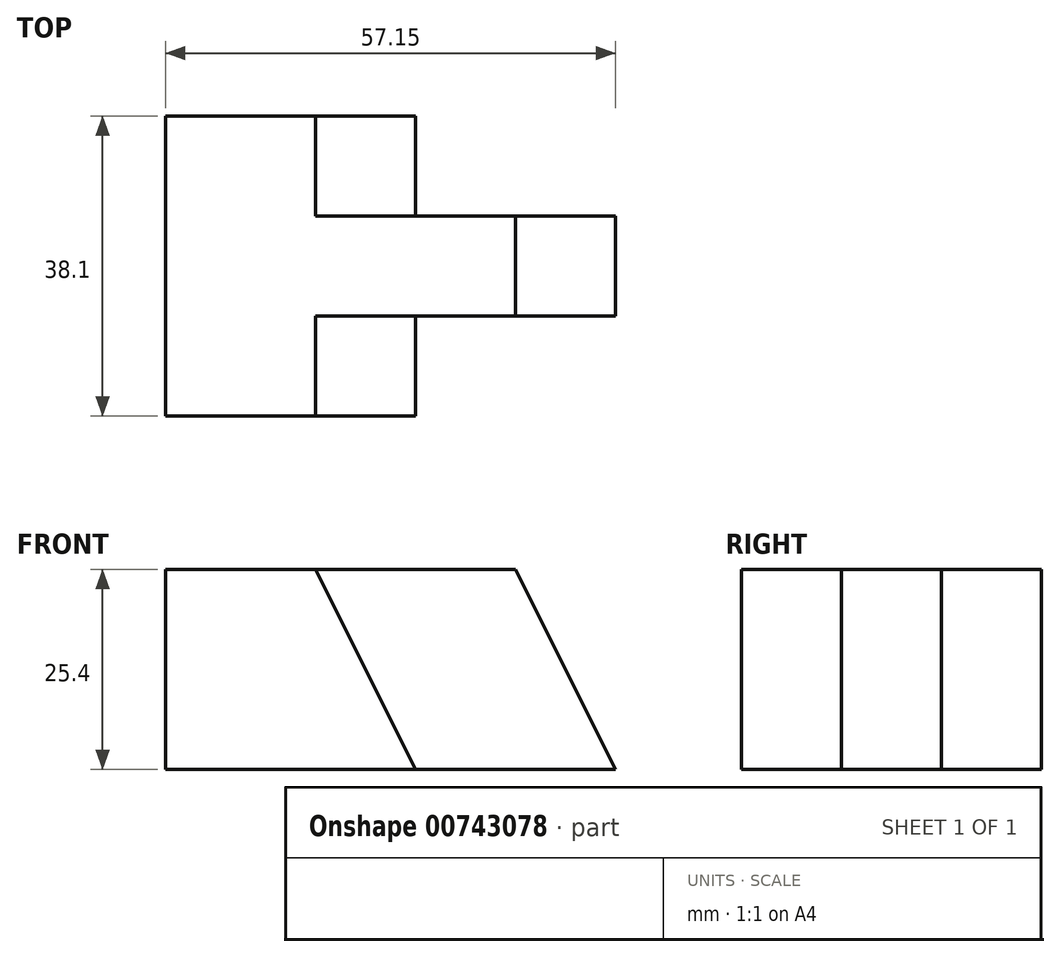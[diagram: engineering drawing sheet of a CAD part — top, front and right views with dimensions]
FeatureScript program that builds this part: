
annotation { "Feature Type Name" : "Feature", "Feature Type Description" : "" }
export const myFeature = defineFeature(function(context is Context, id is Id, definition is map)
    precondition{}
    {
        {
            var Q0;
            Q0=qCreatedBy(makeId("Top.planeOp"),FACE);
            var sketch = newSketch(context, id + "F0", { "sketchPlane" : qUnion([Q0])});
            skLineSegment(sketch, "E0", {"start": v(0, 0) * mm, "end": v(0, 38.1) * mm});
            skLineSegment(sketch, "E1", {"start": v(0, 38.1) * mm, "end": v(57.15, 38.1) * mm});
            skLineSegment(sketch, "E2", {"start": v(57.15, 38.1) * mm, "end": v(57.15, 0) * mm});
            skLineSegment(sketch, "E3", {"start": v(57.15, 0) * mm, "end": v(0, 0) * mm});
            skSolve(sketch);
        }
        {
            var Q0;
            Q0=makeQuery(id+"F0.imprint","IMPRINT",FACE,{"disambiguationData":[TD([[makeQuery(id+"F0.imprint","IMPRINT",EDGE,{"derivedFrom":sQuery(id+"F0.wireOp",EDGE,"E0")}),-1.0]])]});
            extrude(context, id + "F1", {"entities" : qUnion([Q0]), "depth" : 25.4 * mm, "offsetDistance" : 25.4 * mm});
        }
        {
            var Q0;
            Q0=makeQuery(id+"F1.opExtrude","SWEPT_FACE",FACE,{"disambiguationData":[OSD([sQuery(id+"F0.wireOp",EDGE,"E3")])]});
            var sketch = newSketch(context, id + "F2", { "sketchPlane" : qUnion([Q0])});
            skLineSegment(sketch, "E4", {"start": v(19.05, 25.4) * mm, "end": v(31.75, 0) * mm});
            skSolve(sketch);
        }
        {
            var Q0;
            {var subQ0=sQuery(id+"F2.wireOp",EDGE,"E4");Q0=makeQuery(id+"F2.imprint","IMPRINT",FACE,{"disambiguationData":[TD([[makeQuery(id+"F2.imprint","IMPRINT",EDGE,{"derivedFrom":subQ0}),1.0]])]});}
            extrude(context, id + "F3", {"entities" : qUnion([Q0]), "operationType" : NewBodyOperationType.REMOVE, "oppositeDirection" : true, "depth" : 12.7 * mm, "offsetDistance" : 25.4 * mm});
        }
        {
            var Q0;
            Q0=makeQuery(id+"F1.opExtrude","SWEPT_FACE",FACE,{"disambiguationData":[OSD([sQuery(id+"F0.wireOp",EDGE,"E1")])]});
            var sketch = newSketch(context, id + "F4", { "sketchPlane" : qUnion([Q0])});
            skLineSegment(sketch, "E5", {"start": v(-19.05, 25.4) * mm, "end": v(-31.75, 0) * mm});
            skSolve(sketch);
        }
        {
            var Q0;
            {var subQ0=sQuery(id+"F4.wireOp",EDGE,"E5");Q0=makeQuery(id+"F4.imprint","IMPRINT",FACE,{"disambiguationData":[TD([[makeQuery(id+"F4.imprint","IMPRINT",EDGE,{"derivedFrom":subQ0}),-1.0]])]});}
            extrude(context, id + "F5", {"entities" : qUnion([Q0]), "operationType" : NewBodyOperationType.REMOVE, "oppositeDirection" : true, "depth" : 12.7 * mm, "offsetDistance" : 25.4 * mm});
        }
        {
            var Q0;
            Q0=makeQuery(id+"F3.boolean.opBoolean","COPY",FACE,{"derivedFrom":makeQuery(id+"F3.opExtrude","CAP_FACE",FACE,{"disambiguationData":[OSD([sQuery(id+"F0.wireOp",EDGE,"E2"),sQuery(id+"F0.wireOp",EDGE,"E3"),sQuery(id+"F2.wireOp",EDGE,"E4")])],"isStart":false})});
            var sketch = newSketch(context, id + "F6", { "sketchPlane" : qUnion([Q0])});
            skLineSegment(sketch, "E6", {"start": v(44.45, 25.4) * mm, "end": v(57.15, 0) * mm});
            skSolve(sketch);
        }
        {
            var Q0;
            {var subQ0=sQuery(id+"F6.wireOp",EDGE,"E6");Q0=makeQuery(id+"F6.imprint","IMPRINT",FACE,{"disambiguationData":[TD([[makeQuery(id+"F6.imprint","IMPRINT",EDGE,{"derivedFrom":subQ0}),1.0]])]});}
            extrude(context, id + "F7", {"entities" : qUnion([Q0]), "operationType" : NewBodyOperationType.REMOVE, "oppositeDirection" : true, "depth" : 25.4 * mm, "offsetDistance" : 25.4 * mm});
        }
    });
